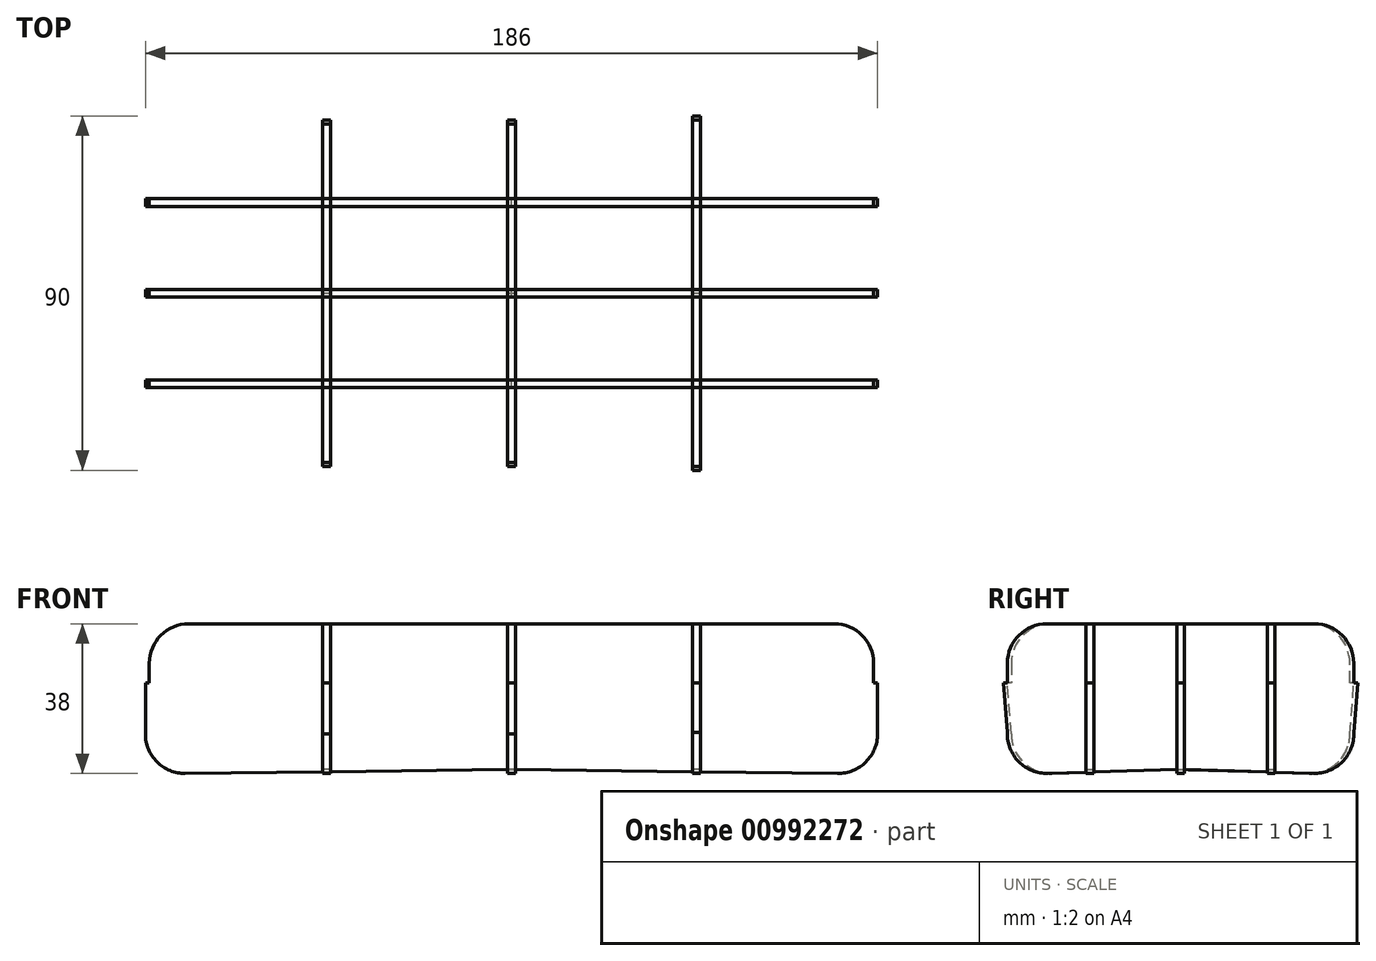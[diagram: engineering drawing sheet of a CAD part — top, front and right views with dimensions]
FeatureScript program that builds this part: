
annotation { "Feature Type Name" : "Feature", "Feature Type Description" : "" }
export const myFeature = defineFeature(function(context is Context, id is Id, definition is map)
    precondition{}
    {
        {
            var Q0;
            Q0=qCreatedBy(makeId("Right.planeOp"),FACE);
            cPlane(context, id + "F0", {"entities" : qUnion([Q0]), "cplaneType" : CPlaneType.OFFSET, "offset" : 47 * mm, "width" : 150 * mm, "height" : 150 * mm});
        }
        {
            var Q0;
            Q0=qCreatedBy(makeId("Right.planeOp"),FACE);
            cPlane(context, id + "F1", {"entities" : qUnion([Q0]), "cplaneType" : CPlaneType.OFFSET, "offset" : 47 * mm, "oppositeDirection" : true, "width" : 150 * mm, "height" : 150 * mm});
        }
        {
            var Q0;
            Q0=qCreatedBy(makeId("Front.planeOp"),FACE);
            cPlane(context, id + "F2", {"entities" : qUnion([Q0]), "cplaneType" : CPlaneType.OFFSET, "offset" : 23 * mm, "width" : 150 * mm, "height" : 150 * mm});
        }
        {
            var Q0;
            Q0=qCreatedBy(makeId("Front.planeOp"),FACE);
            cPlane(context, id + "F3", {"entities" : qUnion([Q0]), "cplaneType" : CPlaneType.OFFSET, "offset" : 23 * mm, "oppositeDirection" : true, "width" : 150 * mm, "height" : 150 * mm});
        }
        {
            var Q0;
            Q0=qCreatedBy(id+"F2.planeOp",FACE);
            var sketch = newSketch(context, id + "F4", { "sketchPlane" : qUnion([Q0])});
            skLineSegment(sketch, "E0", {"start": v(93, -6) * mm, "end": v(93, 7) * mm});
            skLineSegment(sketch, "E1", {"start": v(93, 7) * mm, "end": v(92, 7) * mm});
            skLineSegment(sketch, "E2", {"start": v(92, 7) * mm, "end": v(92, 12) * mm});
            skLineSegment(sketch, "E3", {"start": v(82, 22) * mm, "end": v(-82, 22) * mm});
            skLineSegment(sketch, "E4", {"start": v(-92, 12) * mm, "end": v(-92, 7) * mm});
            skLineSegment(sketch, "E5", {"start": v(-92, 7) * mm, "end": v(-93, 7) * mm});
            skLineSegment(sketch, "E6", {"start": v(-93, 7) * mm, "end": v(-93, -6) * mm});
            skPoint(sketch, "E7.visualSharp", {"position": v(-93, -24.77) * mm});
            skArc(sketch, "E7.filletArc", {"start": v(-93, -6) * mm, "mid": v(-90.03, -13.11) * mm, "end": v(-82.88, -16) * mm});
            skPoint(sketch, "E8.visualSharp", {"position": v(93, -24.77) * mm});
            skArc(sketch, "E8.filletArc", {"start": v(82.88, -16) * mm, "mid": v(90.03, -13.11) * mm, "end": v(93, -6) * mm});
            skPoint(sketch, "E9.visualSharp", {"position": v(-92, 22) * mm});
            skArc(sketch, "E9.filletArc", {"start": v(-82, 22) * mm, "mid": v(-89.07, 19.07) * mm, "end": v(-92, 12) * mm});
            skPoint(sketch, "E10.visualSharp", {"position": v(92, 22) * mm});
            skArc(sketch, "E10.filletArc", {"start": v(92, 12) * mm, "mid": v(89.07, 19.07) * mm, "end": v(82, 22) * mm});
            skLineSegment(sketch, "E11", {"start": v(-82.88, -16) * mm, "end": v(0, -15) * mm});
            skLineSegment(sketch, "E12", {"start": v(0, -15) * mm, "end": v(82.88, -16) * mm});
            skSolve(sketch);
        }
        {
            var Q0;
            Q0=qCreatedBy(makeId("Front.planeOp"),FACE);
            var sketch = newSketch(context, id + "F5", { "sketchPlane" : qUnion([Q0])});
            skLineSegment(sketch, "E13", {"start": v(93, -6) * mm, "end": v(93, 7) * mm});
            skLineSegment(sketch, "E14", {"start": v(93, 7) * mm, "end": v(92, 7) * mm});
            skLineSegment(sketch, "E15", {"start": v(92, 7) * mm, "end": v(92, 12) * mm});
            skLineSegment(sketch, "E16", {"start": v(82, 22) * mm, "end": v(-82, 22) * mm});
            skLineSegment(sketch, "E17", {"start": v(-92, 12) * mm, "end": v(-92, 7) * mm});
            skLineSegment(sketch, "E18", {"start": v(-92, 7) * mm, "end": v(-93, 7) * mm});
            skLineSegment(sketch, "E19", {"start": v(-93, 7) * mm, "end": v(-93, -6) * mm});
            skPoint(sketch, "E20.visualSharp", {"position": v(-93, -24.77) * mm});
            skArc(sketch, "E20.filletArc", {"start": v(-93, -6) * mm, "mid": v(-90.03, -13.11) * mm, "end": v(-82.88, -16) * mm});
            skPoint(sketch, "E21.visualSharp", {"position": v(93, -24.77) * mm});
            skArc(sketch, "E21.filletArc", {"start": v(82.88, -16) * mm, "mid": v(90.03, -13.11) * mm, "end": v(93, -6) * mm});
            skPoint(sketch, "E22.visualSharp", {"position": v(-92, 22) * mm});
            skArc(sketch, "E22.filletArc", {"start": v(-82, 22) * mm, "mid": v(-89.07, 19.07) * mm, "end": v(-92, 12) * mm});
            skPoint(sketch, "E23.visualSharp", {"position": v(92, 22) * mm});
            skArc(sketch, "E23.filletArc", {"start": v(92, 12) * mm, "mid": v(89.07, 19.07) * mm, "end": v(82, 22) * mm});
            skLineSegment(sketch, "E24", {"start": v(-82.88, -16) * mm, "end": v(0, -15) * mm});
            skLineSegment(sketch, "E25", {"start": v(0, -15) * mm, "end": v(82.88, -16) * mm});
            skSolve(sketch);
        }
        {
            var Q0;
            Q0=qCreatedBy(id+"F3.planeOp",FACE);
            var sketch = newSketch(context, id + "F6", { "sketchPlane" : qUnion([Q0])});
            skLineSegment(sketch, "E26", {"start": v(93, -6) * mm, "end": v(93, 7) * mm});
            skLineSegment(sketch, "E27", {"start": v(93, 7) * mm, "end": v(92, 7) * mm});
            skLineSegment(sketch, "E28", {"start": v(92, 7) * mm, "end": v(92, 12) * mm});
            skLineSegment(sketch, "E29", {"start": v(82, 22) * mm, "end": v(-82, 22) * mm});
            skLineSegment(sketch, "E30", {"start": v(-92, 12) * mm, "end": v(-92, 7) * mm});
            skLineSegment(sketch, "E31", {"start": v(-92, 7) * mm, "end": v(-93, 7) * mm});
            skLineSegment(sketch, "E32", {"start": v(-93, 7) * mm, "end": v(-93, -6) * mm});
            skPoint(sketch, "E33.visualSharp", {"position": v(-93, -24.77) * mm});
            skArc(sketch, "E33.filletArc", {"start": v(-93, -6) * mm, "mid": v(-90.03, -13.11) * mm, "end": v(-82.88, -16) * mm});
            skPoint(sketch, "E34.visualSharp", {"position": v(93, -24.77) * mm});
            skArc(sketch, "E34.filletArc", {"start": v(82.88, -16) * mm, "mid": v(90.03, -13.11) * mm, "end": v(93, -6) * mm});
            skPoint(sketch, "E35.visualSharp", {"position": v(-92, 22) * mm});
            skArc(sketch, "E35.filletArc", {"start": v(-82, 22) * mm, "mid": v(-89.07, 19.07) * mm, "end": v(-92, 12) * mm});
            skPoint(sketch, "E36.visualSharp", {"position": v(92, 22) * mm});
            skArc(sketch, "E36.filletArc", {"start": v(92, 12) * mm, "mid": v(89.07, 19.07) * mm, "end": v(82, 22) * mm});
            skLineSegment(sketch, "E37", {"start": v(-82.88, -16) * mm, "end": v(0, -15) * mm});
            skLineSegment(sketch, "E38", {"start": v(0, -15) * mm, "end": v(82.88, -16) * mm});
            skSolve(sketch);
        }
        {
            var Q0;
            Q0=qCreatedBy(id+"F0.planeOp",FACE);
            var sketch = newSketch(context, id + "F7", { "sketchPlane" : qUnion([Q0])});
            skLineSegment(sketch, "E39", {"start": v(45, 7) * mm, "end": v(44, 7) * mm});
            skLineSegment(sketch, "E40", {"start": v(44, 7) * mm, "end": v(44, 12) * mm});
            skLineSegment(sketch, "E41", {"start": v(34, 22) * mm, "end": v(-34, 22) * mm});
            skLineSegment(sketch, "E42", {"start": v(-44, 12) * mm, "end": v(-44, 7) * mm});
            skLineSegment(sketch, "E43", {"start": v(-44, 7) * mm, "end": v(-45, 7) * mm});
            skPoint(sketch, "E44.visualSharp", {"position": v(-42.5, -26.61) * mm});
            skArc(sketch, "E44.filletArc", {"start": v(-44, -5.64) * mm, "mid": v(-41.1, -13.05) * mm, "end": v(-33.71, -16) * mm});
            skPoint(sketch, "E45.visualSharp", {"position": v(42.5, -26.61) * mm});
            skArc(sketch, "E45.filletArc", {"start": v(33.7, -16) * mm, "mid": v(41.09, -13.06) * mm, "end": v(44, -5.67) * mm});
            skPoint(sketch, "E46.visualSharp", {"position": v(-44, 22) * mm});
            skArc(sketch, "E46.filletArc", {"start": v(-34, 22) * mm, "mid": v(-41.07, 19.07) * mm, "end": v(-44, 12) * mm});
            skPoint(sketch, "E47.visualSharp", {"position": v(44, 22) * mm});
            skArc(sketch, "E47.filletArc", {"start": v(44, 12) * mm, "mid": v(41.07, 19.07) * mm, "end": v(34, 22) * mm});
            skLineSegment(sketch, "E48", {"start": v(-33.71, -16) * mm, "end": v(-0.13, -15) * mm});
            skLineSegment(sketch, "E49", {"start": v(-0.13, -15) * mm, "end": v(33.7, -16) * mm});
            skLineSegment(sketch, "E50", {"start": v(44, -5.67) * mm, "end": v(45, 7) * mm});
            skLineSegment(sketch, "E51", {"start": v(-44, -5.64) * mm, "end": v(-45, 7) * mm});
            skSolve(sketch);
        }
        {
            var Q0;
            Q0=qCreatedBy(id+"F1.planeOp",FACE);
            var sketch = newSketch(context, id + "F8", { "sketchPlane" : qUnion([Q0])});
            skLineSegment(sketch, "E52", {"start": v(44, 7) * mm, "end": v(43, 7) * mm});
            skLineSegment(sketch, "E53", {"start": v(43, 7) * mm, "end": v(43, 12) * mm});
            skLineSegment(sketch, "E54", {"start": v(33, 22) * mm, "end": v(-33, 22) * mm});
            skLineSegment(sketch, "E55", {"start": v(-43, 12) * mm, "end": v(-43, 7) * mm});
            skLineSegment(sketch, "E56", {"start": v(-43, 7) * mm, "end": v(-44, 7) * mm});
            skPoint(sketch, "E57.visualSharp", {"position": v(-42.5, -28.24) * mm});
            skArc(sketch, "E57.filletArc", {"start": v(-43, -5.97) * mm, "mid": v(-39.97, -13.17) * mm, "end": v(-32.7, -16) * mm});
            skPoint(sketch, "E58.visualSharp", {"position": v(42.5, -28.24) * mm});
            skArc(sketch, "E58.filletArc", {"start": v(32.7, -16) * mm, "mid": v(39.98, -13.17) * mm, "end": v(43, -5.98) * mm});
            skPoint(sketch, "E59.visualSharp", {"position": v(-43, 22) * mm});
            skArc(sketch, "E59.filletArc", {"start": v(-33, 22) * mm, "mid": v(-40.07, 19.07) * mm, "end": v(-43, 12) * mm});
            skPoint(sketch, "E60.visualSharp", {"position": v(43, 22) * mm});
            skArc(sketch, "E60.filletArc", {"start": v(43, 12) * mm, "mid": v(40.07, 19.07) * mm, "end": v(33, 22) * mm});
            skLineSegment(sketch, "E61", {"start": v(-32.7, -16) * mm, "end": v(-0.06, -15) * mm});
            skLineSegment(sketch, "E62", {"start": v(-0.06, -15) * mm, "end": v(32.7, -16) * mm});
            skLineSegment(sketch, "E63", {"start": v(43, -5.98) * mm, "end": v(44, 7) * mm});
            skLineSegment(sketch, "E64", {"start": v(-43, -5.97) * mm, "end": v(-44, 7) * mm});
            skSolve(sketch);
        }
        {
            var Q0;
            Q0=qCreatedBy(makeId("Right.planeOp"),FACE);
            var sketch = newSketch(context, id + "F9", { "sketchPlane" : qUnion([Q0])});
            skLineSegment(sketch, "E65", {"start": v(44, 7) * mm, "end": v(43, 7) * mm});
            skLineSegment(sketch, "E66", {"start": v(43, 7) * mm, "end": v(43, 12) * mm});
            skLineSegment(sketch, "E67", {"start": v(33, 22) * mm, "end": v(-33, 22) * mm});
            skLineSegment(sketch, "E68", {"start": v(-43, 12) * mm, "end": v(-43, 7) * mm});
            skLineSegment(sketch, "E69", {"start": v(-43, 7) * mm, "end": v(-44, 7) * mm});
            skPoint(sketch, "E70.visualSharp", {"position": v(-42.5, -29.68) * mm});
            skArc(sketch, "E70.filletArc", {"start": v(-43, -5.97) * mm, "mid": v(-39.97, -13.17) * mm, "end": v(-32.69, -16) * mm});
            skPoint(sketch, "E71.visualSharp", {"position": v(42.5, -29.68) * mm});
            skArc(sketch, "E71.filletArc", {"start": v(32.7, -16) * mm, "mid": v(39.98, -13.17) * mm, "end": v(43, -5.98) * mm});
            skPoint(sketch, "E72.visualSharp", {"position": v(-43, 22) * mm});
            skArc(sketch, "E72.filletArc", {"start": v(-33, 22) * mm, "mid": v(-40.07, 19.07) * mm, "end": v(-43, 12) * mm});
            skPoint(sketch, "E73.visualSharp", {"position": v(43, 22) * mm});
            skArc(sketch, "E73.filletArc", {"start": v(43, 12) * mm, "mid": v(40.07, 19.07) * mm, "end": v(33, 22) * mm});
            skLineSegment(sketch, "E74", {"start": v(-32.69, -16) * mm, "end": v(-0.06, -15) * mm});
            skLineSegment(sketch, "E75", {"start": v(-0.06, -15) * mm, "end": v(32.7, -16) * mm});
            skLineSegment(sketch, "E76", {"start": v(43, -5.98) * mm, "end": v(44, 7) * mm});
            skLineSegment(sketch, "E77", {"start": v(-43, -5.97) * mm, "end": v(-44, 7) * mm});
            skSolve(sketch);
        }
        {
            var Q0;
            Q0=makeQuery(id+"F4.imprint","IMPRINT",FACE,{"disambiguationData":[TD([[makeQuery(id+"F4.imprint","IMPRINT",EDGE,{"derivedFrom":sQuery(id+"F4.wireOp",EDGE,"E0")}),1.0]])]});
            extrude(context, id + "F10", {"entities" : qUnion([Q0]), "endBound" : BoundingType.SYMMETRIC, "depth" : 2 * mm, "offsetDistance" : 25 * mm});
        }
        {
            var Q0;
            Q0=makeQuery(id+"F5.imprint","IMPRINT",FACE,{"disambiguationData":[TD([[makeQuery(id+"F5.imprint","IMPRINT",EDGE,{"derivedFrom":sQuery(id+"F5.wireOp",EDGE,"E13")}),1.0]])]});
            var Q1;
            Q1=makeQuery(id+"F6.imprint","IMPRINT",FACE,{"disambiguationData":[TD([[makeQuery(id+"F6.imprint","IMPRINT",EDGE,{"derivedFrom":sQuery(id+"F6.wireOp",EDGE,"E26")}),1.0]])]});
            extrude(context, id + "F11", {"entities" : qUnion([Q0, Q1]), "endBound" : BoundingType.SYMMETRIC, "depth" : 2 * mm, "offsetDistance" : 25 * mm});
        }
        {
            var Q0;
            Q0=makeQuery(id+"F8.imprint","IMPRINT",FACE,{"disambiguationData":[TD([[makeQuery(id+"F8.imprint","IMPRINT",EDGE,{"derivedFrom":sQuery(id+"F8.wireOp",EDGE,"E52")}),1.0]])]});
            var Q1;
            Q1=makeQuery(id+"F9.imprint","IMPRINT",FACE,{"disambiguationData":[TD([[makeQuery(id+"F9.imprint","IMPRINT",EDGE,{"derivedFrom":sQuery(id+"F9.wireOp",EDGE,"E65")}),1.0]])]});
            var Q2;
            Q2=makeQuery(id+"F7.imprint","IMPRINT",FACE,{"disambiguationData":[TD([[makeQuery(id+"F7.imprint","IMPRINT",EDGE,{"derivedFrom":sQuery(id+"F7.wireOp",EDGE,"E39")}),1.0]])]});
            extrude(context, id + "F12", {"entities" : qUnion([Q0, Q1, Q2]), "endBound" : BoundingType.SYMMETRIC, "depth" : 2 * mm, "offsetDistance" : 25 * mm});
        }
    });
